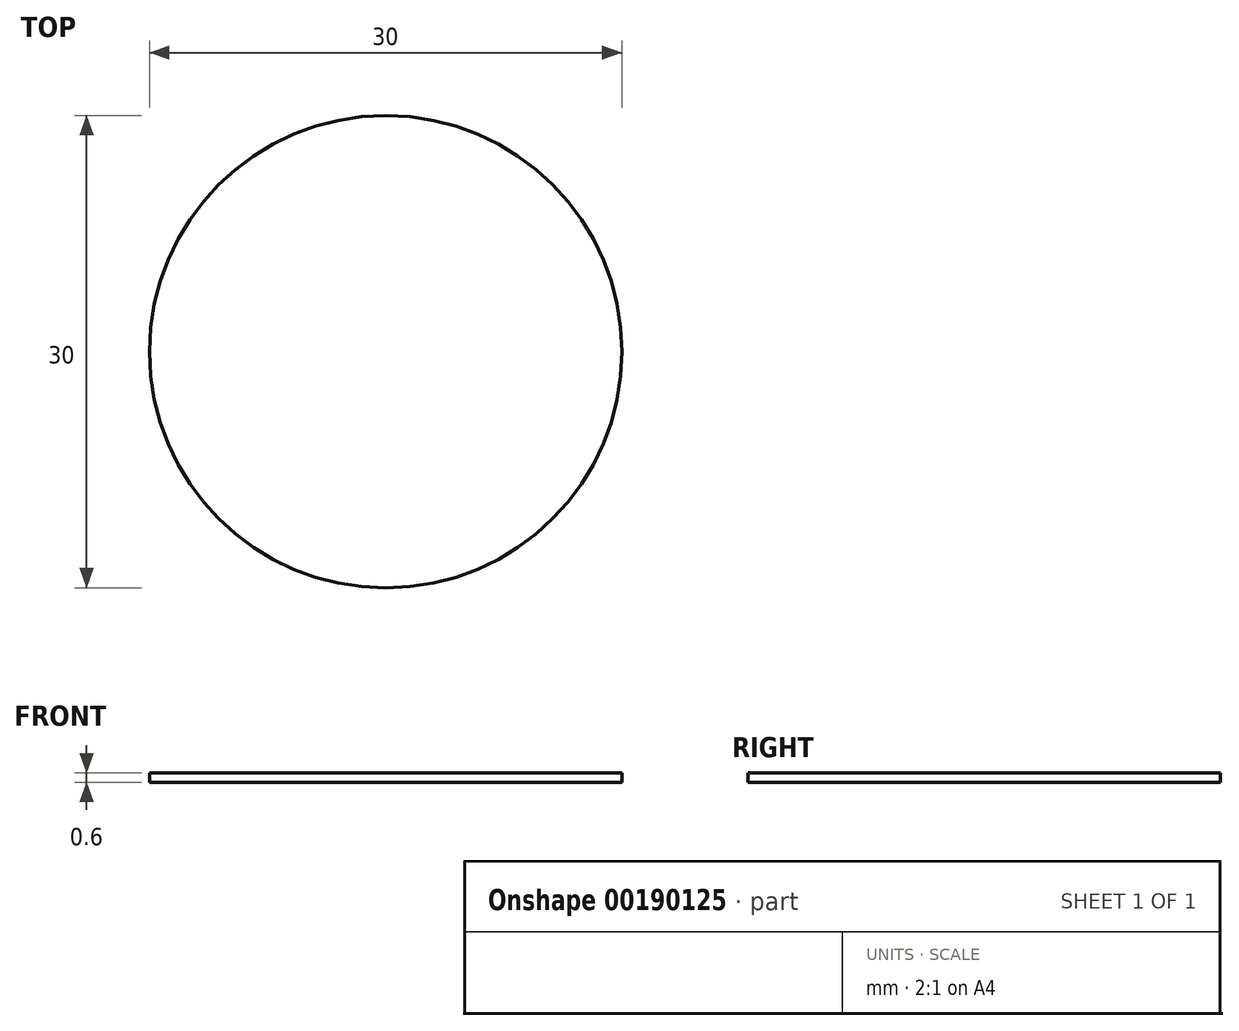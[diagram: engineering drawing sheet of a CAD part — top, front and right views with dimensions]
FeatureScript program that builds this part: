
annotation { "Feature Type Name" : "Feature", "Feature Type Description" : "" }
export const myFeature = defineFeature(function(context is Context, id is Id, definition is map)
    precondition{}
    {
        {
            var Q0;
            Q0=qCreatedBy(makeId("Top.planeOp"),FACE);
            var sketch = newSketch(context, id + "F0", { "sketchPlane" : qUnion([Q0])});
            skCircle(sketch, "E0", {"center": v(0, 0) * mm, "radius": 15 * mm});
            skSolve(sketch);
        }
        {
            var Q0;
            Q0 = qSketchRegion(id + "F0", true);
            extrude(context, id + "F1", {"entities" : qUnion([Q0]), "depth" : 0.6 * mm, "offsetDistance" : 25 * mm});
        }
    });
